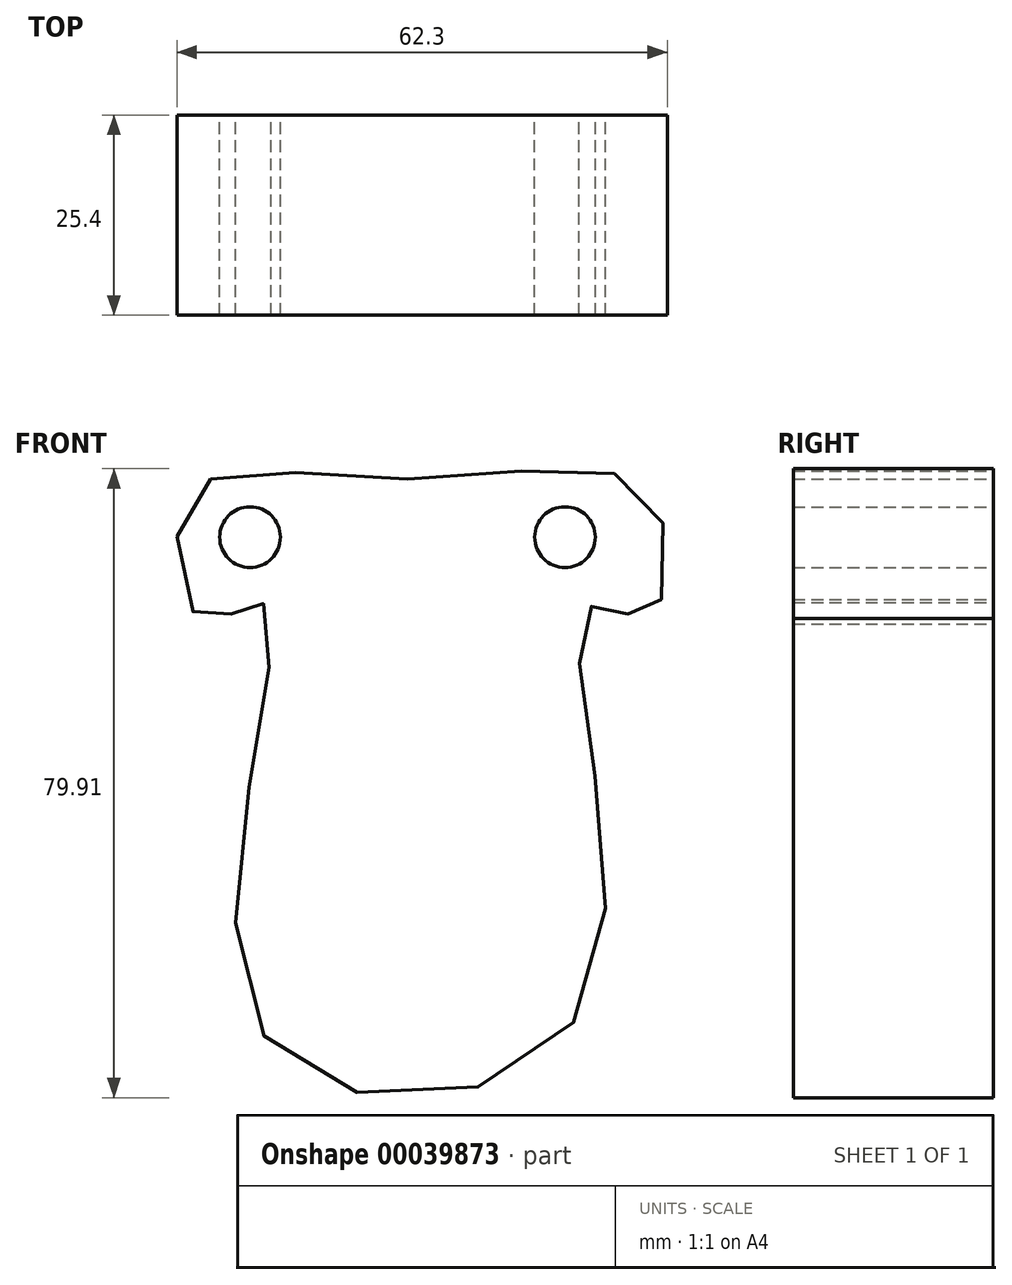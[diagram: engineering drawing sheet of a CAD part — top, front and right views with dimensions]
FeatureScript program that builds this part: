
annotation { "Feature Type Name" : "Feature", "Feature Type Description" : "" }
export const myFeature = defineFeature(function(context is Context, id is Id, definition is map)
    precondition{}
    {
        {
            var Q0;
            Q0=qCreatedBy(makeId("Front.planeOp"),FACE);
            var sketch = newSketch(context, id + "F0", { "sketchPlane" : qUnion([Q0])});
            skFitSpline(sketch, "E0", {"points": [v(0, 56.4) * mm, v(30.87, 54.18) * mm, v(30.67, 38.84) * mm, v(25.02, 40.66) * mm, v(21.8, 35.62) * mm, v(20.99, -12.81) * mm, v(-17.76, -15.03) * mm, v(-17.35, 35.62) * mm, v(-19.78, 41.06) * mm, v(-25.63, 38.04) * mm, v(-28.05, 53.78) * mm, v(0, 56.4) * mm]});
            skSolve(sketch);
        }
        {
            var Q0;
            Q0=makeQuery(id+"F0.imprint","IMPRINT",FACE,{"disambiguationData":[TD([[makeQuery(id+"F0.imprint","IMPRINT",EDGE,{"derivedFrom":sQuery(id+"F0.wireOp",EDGE,"E0")}),-1.0]])]});
            extrude(context, id + "F1", {"entities" : qUnion([Q0]), "depth" : 25.4 * mm});
        }
        {
            var Q0;
            Q0=makeQuery(id+"F1.opExtrude","CAP_FACE",FACE,{"disambiguationData":[OSD([sQuery(id+"F0.wireOp",EDGE,"E0")])],"isStart":true});
            var sketch = newSketch(context, id + "F2", { "sketchPlane" : qUnion([Q0])});
            skCircle(sketch, "E1", {"center": v(20, 49.01) * mm, "radius": 3.86 * mm});
            skCircle(sketch, "E2.MirrorC", {"center": v(-20, 49.01) * mm, "radius": 3.86 * mm});
            skSolve(sketch);
        }
        {
            var Q0;
            Q0 = qSketchRegion(id + "F2", true);
            extrude(context, id + "F3", {"entities" : qUnion([Q0]), "operationType" : NewBodyOperationType.REMOVE, "oppositeDirection" : true, "depth" : 25.4 * mm});
        }
    });
